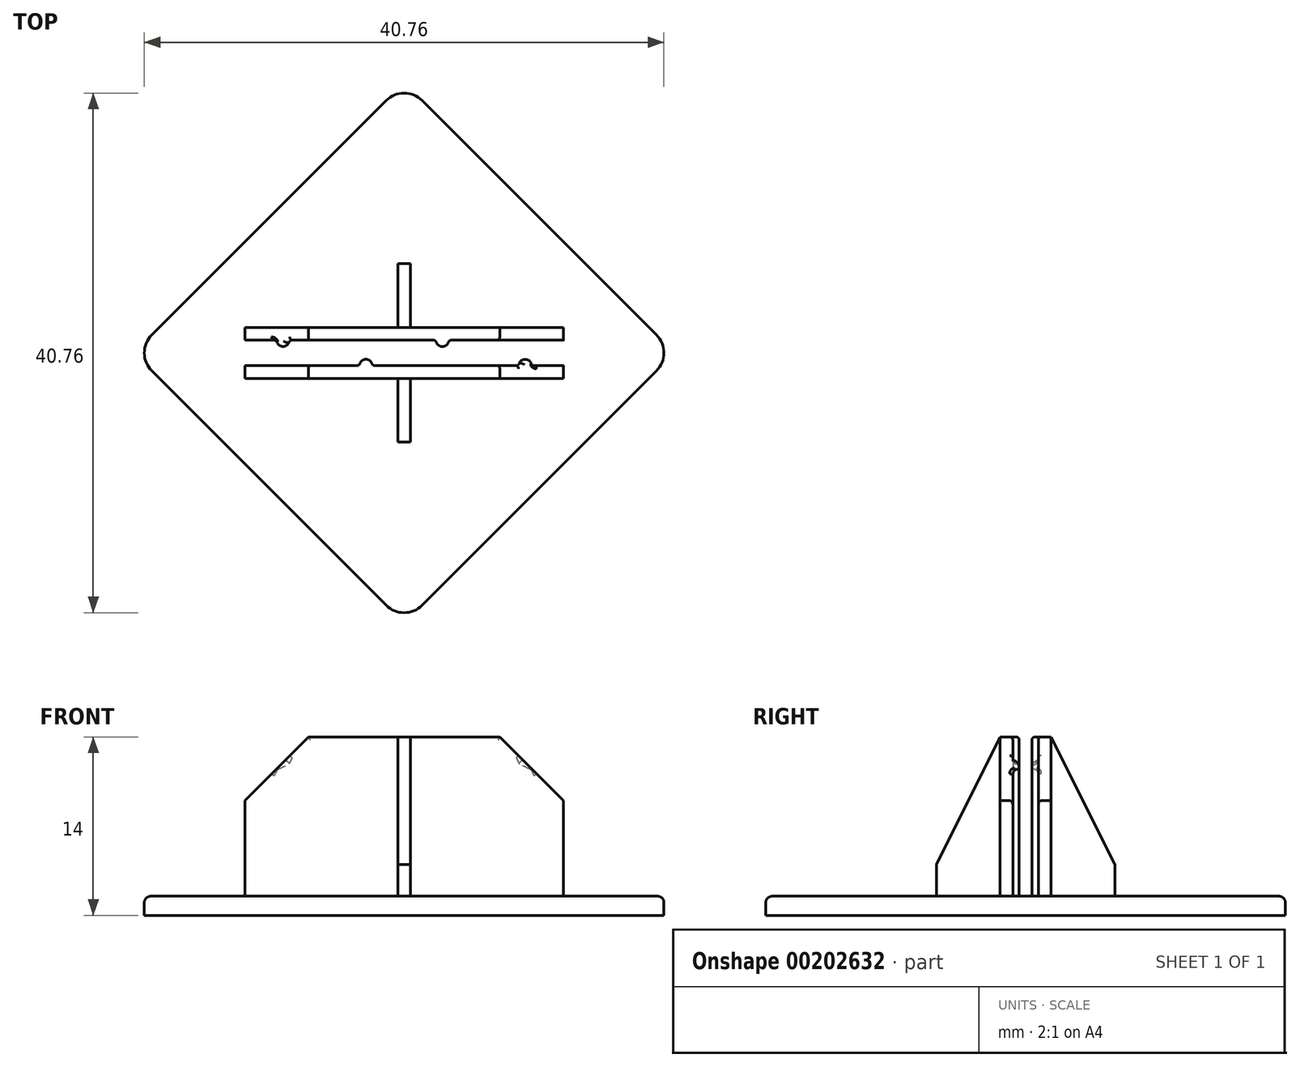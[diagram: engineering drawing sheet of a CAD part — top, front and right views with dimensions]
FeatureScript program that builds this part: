
annotation { "Feature Type Name" : "Feature", "Feature Type Description" : "" }
export const myFeature = defineFeature(function(context is Context, id is Id, definition is map)
    precondition{}
    {
        {
            var Q0;
            Q0=qCreatedBy(makeId("Front.planeOp"),FACE);
            var sketch = newSketch(context, id + "F0", { "sketchPlane" : qUnion([Q0])});
            skLineSegment(sketch, "E0", {"start": v(0, 0) * mm, "end": v(0, 22.97) * mm, "construction": true});
            skSolve(sketch);
        }
        {
            var Q0;
            Q0=qCreatedBy(makeId("Top.planeOp"),FACE);
            var sketch = newSketch(context, id + "F1", { "sketchPlane" : qUnion([Q0])});
            skLineSegment(sketch, "E1.bottom", {"start": v(15, -15) * mm, "end": v(-15, -15) * mm});
            skLineSegment(sketch, "E1.top", {"start": v(15, 15) * mm, "end": v(-15, 15) * mm});
            skLineSegment(sketch, "E1.left", {"start": v(15, -15) * mm, "end": v(15, 15) * mm});
            skLineSegment(sketch, "E1.right", {"start": v(-15, -15) * mm, "end": v(-15, 15) * mm});
            skPoint(sketch, "E1.middle", {"position": v(0, 0) * mm});
            skSolve(sketch);
        }
        {
            var Q0;
            Q0=makeQuery(id+"F1.imprint","IMPRINT",FACE,{"disambiguationData":[TD([[makeQuery(id+"F1.imprint","IMPRINT",EDGE,{"derivedFrom":sQuery(id+"F1.wireOp",EDGE,"E1.bottom")}),-1.0]])]});
            extrude(context, id + "F2", {"entities" : qUnion([Q0]), "depth" : 1.5 * mm});
        }
        {
            var Q0;
            Q0=makeQuery(id+"F2.opExtrude","SWEPT_BODY",BODY,{"disambiguationData":[OSD([sQuery(id+"F1.wireOp",EDGE,"E1.bottom"),sQuery(id+"F1.wireOp",EDGE,"E1.top"),sQuery(id+"F1.wireOp",EDGE,"E1.left"),sQuery(id+"F1.wireOp",EDGE,"E1.right")])]});
            var Q1;
            Q1=sQuery(id+"F0.wireOp",EDGE,"E0");
            transform(context, id + "F3", {"entities" : qUnion([Q0]), "transformType" : TransformType.ROTATION, "transformAxis" : qUnion([Q1]), "angle" : 45 * degree, "makeCopy" : false});
        }
        {
            var Q0;
            Q0=makeQuery(id+"F2.opExtrude","SWEPT_EDGE",EDGE,{"disambiguationData":[OSD([sQuery(id+"F1.wireOp",EDGE,"E1.top"),sQuery(id+"F1.wireOp",EDGE,"E1.right")])]});
            var Q1;
            Q1=makeQuery(id+"F2.opExtrude","SWEPT_EDGE",EDGE,{"disambiguationData":[OSD([sQuery(id+"F1.wireOp",EDGE,"E1.bottom"),sQuery(id+"F1.wireOp",EDGE,"E1.right")])]});
            var Q2;
            Q2=makeQuery(id+"F2.opExtrude","SWEPT_EDGE",EDGE,{"disambiguationData":[OSD([sQuery(id+"F1.wireOp",EDGE,"E1.bottom"),sQuery(id+"F1.wireOp",EDGE,"E1.left")])]});
            var Q3;
            Q3=makeQuery(id+"F2.opExtrude","SWEPT_EDGE",EDGE,{"disambiguationData":[OSD([sQuery(id+"F1.wireOp",EDGE,"E1.top"),sQuery(id+"F1.wireOp",EDGE,"E1.left")])]});
            fillet(context, id + "F4", {"entities" : qUnion([Q0, Q1, Q2, Q3]), "radius" : 2 * mm, "tangentPropagation" : true, "allowEdgeOverflow" : false});
        }
        {
            var Q0;
            Q0=makeQuery(id+"F2.opExtrude","CAP_FACE",FACE,{"disambiguationData":[OSD([sQuery(id+"F1.wireOp",EDGE,"E1.bottom"),sQuery(id+"F1.wireOp",EDGE,"E1.top"),sQuery(id+"F1.wireOp",EDGE,"E1.left"),sQuery(id+"F1.wireOp",EDGE,"E1.right")])],"isStart":false});
            fillet(context, id + "F5", {"entities" : qUnion([Q0]), "radius" : .5 * mm, "tangentPropagation" : true, "allowEdgeOverflow" : false});
        }
        {
            var Q0;
            Q0=makeQuery(id+"F2.opExtrude","CAP_FACE",FACE,{"disambiguationData":[OSD([sQuery(id+"F1.wireOp",EDGE,"E1.bottom"),sQuery(id+"F1.wireOp",EDGE,"E1.top"),sQuery(id+"F1.wireOp",EDGE,"E1.left"),sQuery(id+"F1.wireOp",EDGE,"E1.right")])],"isStart":false});
            var sketch = newSketch(context, id + "F6", { "sketchPlane" : qUnion([Q0])});
            skLineSegment(sketch, "E2", {"start": v(-18.38, 0) * mm, "end": v(18.38, 0) * mm, "construction": true});
            skLineSegment(sketch, "E3.0", {"start": v(-18.38, 1) * mm, "end": v(18.38, 1) * mm, "construction": true});
            skLineSegment(sketch, "E4.0", {"start": v(-18.38, 2) * mm, "end": v(18.38, 2) * mm, "construction": true});
            skLineSegment(sketch, "E5.0", {"start": v(-18.38, 7) * mm, "end": v(18.38, 7) * mm, "construction": true});
            skLineSegment(sketch, "E6", {"start": v(0, 18.38) * mm, "end": v(0, -18.38) * mm, "construction": true});
            skLineSegment(sketch, "E7.0", {"start": v(-12.5, 18.38) * mm, "end": v(-12.5, -18.38) * mm, "construction": true});
            skLineSegment(sketch, "E8.0", {"start": v(12.5, 18.38) * mm, "end": v(12.5, -18.38) * mm, "construction": true});
            skLineSegment(sketch, "E9.0", {"start": v(-0.5, 18.38) * mm, "end": v(-0.5, -18.38) * mm, "construction": true});
            skLineSegment(sketch, "E10.0", {"start": v(0.5, 18.38) * mm, "end": v(0.5, -18.38) * mm, "construction": true});
            skLineSegment(sketch, "E11.0", {"start": v(-9.5, 18.38) * mm, "end": v(-9.5, -18.38) * mm, "construction": true});
            skLineSegment(sketch, "E12.0", {"start": v(3, 18.38) * mm, "end": v(3, -18.38) * mm, "construction": true});
            skCircle(sketch, "E13", {"center": v(-9.5, 1) * mm, "radius": 0.5 * mm});
            skCircle(sketch, "E14", {"center": v(3, 1) * mm, "radius": 0.5 * mm});
            skLineSegment(sketch, "E15", {"start": v(0.5, 7) * mm, "end": v(0.5, 2) * mm});
            skLineSegment(sketch, "E16", {"start": v(0.5, 2) * mm, "end": v(12.5, 2) * mm});
            skLineSegment(sketch, "E17", {"start": v(12.5, 2) * mm, "end": v(12.5, 1) * mm});
            skLineSegment(sketch, "E18", {"start": v(12.5, 1) * mm, "end": v(-12.5, 1) * mm});
            skLineSegment(sketch, "E19", {"start": v(-12.5, 1) * mm, "end": v(-12.5, 2) * mm});
            skLineSegment(sketch, "E20", {"start": v(-12.5, 2) * mm, "end": v(-0.5, 2) * mm});
            skLineSegment(sketch, "E21", {"start": v(-0.5, 2) * mm, "end": v(-0.5, 7) * mm});
            skLineSegment(sketch, "E22", {"start": v(-0.5, 7) * mm, "end": v(0.5, 7) * mm});
            skSolve(sketch);
        }
        {
            var Q0;
            Q0=makeQuery(id+"F6.imprint","IMPRINT",FACE,{"disambiguationData":[TD([[makeQuery(id+"F6.imprint","IMPRINT",EDGE,{"derivedFrom":sQuery(id+"F6.wireOp",EDGE,"E15")}),-1.0]])]});
            var Q1;
            {var subQ0=sQuery(id+"F6.wireOp",EDGE,"E18");var subQ1=sQuery(id+"F6.wireOp",EDGE,"E13");var subQ2=makeQuery(id+"F6.imprint","INTERSECT",VERTEX,{"disambiguationData":[OD(0.0)],"derivedFrom":[subQ1,subQ0]});Q1=makeQuery(id+"F6.imprint","IMPRINT",FACE,{"disambiguationData":[TD([[makeQuery(id+"F6.imprint","IMPRINT",EDGE,{"disambiguationData":[TD([[subQ2,-1.0]])],"derivedFrom":subQ1}),1.0]])]});}
            var Q2;
            {var subQ0=sQuery(id+"F6.wireOp",EDGE,"E18");var subQ1=sQuery(id+"F6.wireOp",EDGE,"E13");var subQ2=makeQuery(id+"F6.imprint","INTERSECT",VERTEX,{"disambiguationData":[OD(0.0)],"derivedFrom":[subQ1,subQ0]});Q2=makeQuery(id+"F6.imprint","IMPRINT",FACE,{"disambiguationData":[TD([[makeQuery(id+"F6.imprint","IMPRINT",EDGE,{"disambiguationData":[TD([[subQ2,1.0]])],"derivedFrom":subQ1}),1.0]])]});}
            var Q3;
            {var subQ0=sQuery(id+"F6.wireOp",EDGE,"E18");var subQ1=sQuery(id+"F6.wireOp",EDGE,"E14");var subQ2=makeQuery(id+"F6.imprint","INTERSECT",VERTEX,{"disambiguationData":[OD(0.0)],"derivedFrom":[subQ1,subQ0]});Q3=makeQuery(id+"F6.imprint","IMPRINT",FACE,{"disambiguationData":[TD([[makeQuery(id+"F6.imprint","IMPRINT",EDGE,{"disambiguationData":[TD([[subQ2,-1.0]])],"derivedFrom":subQ1}),1.0]])]});}
            var Q4;
            {var subQ0=sQuery(id+"F6.wireOp",EDGE,"E18");var subQ1=sQuery(id+"F6.wireOp",EDGE,"E14");var subQ2=makeQuery(id+"F6.imprint","INTERSECT",VERTEX,{"disambiguationData":[OD(0.0)],"derivedFrom":[subQ1,subQ0]});Q4=makeQuery(id+"F6.imprint","IMPRINT",FACE,{"disambiguationData":[TD([[makeQuery(id+"F6.imprint","IMPRINT",EDGE,{"disambiguationData":[TD([[subQ2,1.0]])],"derivedFrom":subQ1}),1.0]])]});}
            extrude(context, id + "F7", {"entities" : qUnion([Q0, Q1, Q2, Q3, Q4]), "depth" : 12.5 * mm});
        }
        {
            var Q0;
            Q0=makeQuery(id+"F7.opExtrude","CAP_EDGE",EDGE,{"disambiguationData":[OSD([sQuery(id+"F6.wireOp",EDGE,"E17")])],"isStart":false});
            var Q1;
            Q1=makeQuery(id+"F7.opExtrude","CAP_EDGE",EDGE,{"disambiguationData":[OSD([sQuery(id+"F6.wireOp",EDGE,"E19")])],"isStart":false});
            chamfer(context, id + "F8", {"entities" : qUnion([Q0, Q1]), "width" : 5 * mm, "tangentPropagation" : true});
        }
        {
            var Q0;
            Q0=makeQuery(id+"F7.opExtrude","CAP_EDGE",EDGE,{"disambiguationData":[OSD([sQuery(id+"F6.wireOp",EDGE,"E22")])],"isStart":false});
            chamfer(context, id + "F9", {"entities" : qUnion([Q0]), "chamferType" : ChamferType.TWO_OFFSETS, "width1" : 10 * mm, "oppositeDirection" : false, "width2" : 5 * mm, "tangentPropagation" : true});
        }
        {
            var Q0;
            {var subQ0=sQuery(id+"F6.wireOp",EDGE,"E18");var subQ1=sQuery(id+"F6.wireOp",EDGE,"E14");Q0=makeQuery(id+"F7.opExtrude","SWEPT_EDGE",EDGE,{"disambiguationData":[OSD([subQ1,subQ0]),TDD([makeQuery(id+"F6.imprint","INTERSECT",VERTEX,{"disambiguationData":[OD(0.0)],"derivedFrom":[subQ1,subQ0]})])]});}
            var Q1;
            {var subQ0=sQuery(id+"F6.wireOp",EDGE,"E18");var subQ1=sQuery(id+"F6.wireOp",EDGE,"E13");Q1=makeQuery(id+"F7.opExtrude","SWEPT_EDGE",EDGE,{"disambiguationData":[OSD([subQ1,subQ0]),TDD([makeQuery(id+"F6.imprint","INTERSECT",VERTEX,{"disambiguationData":[OD(0.0)],"derivedFrom":[subQ1,subQ0]})])]});}
            var Q2;
            {var subQ0=sQuery(id+"F6.wireOp",EDGE,"E18");var subQ1=sQuery(id+"F6.wireOp",EDGE,"E14");Q2=makeQuery(id+"F7.opExtrude","SWEPT_EDGE",EDGE,{"disambiguationData":[OSD([subQ1,subQ0]),TDD([makeQuery(id+"F6.imprint","INTERSECT",VERTEX,{"disambiguationData":[OD(1.0)],"derivedFrom":[subQ1,subQ0]})])]});}
            var Q3;
            {var subQ0=sQuery(id+"F6.wireOp",EDGE,"E18");var subQ1=sQuery(id+"F6.wireOp",EDGE,"E13");Q3=makeQuery(id+"F7.opExtrude","SWEPT_EDGE",EDGE,{"disambiguationData":[OSD([subQ1,subQ0]),TDD([makeQuery(id+"F6.imprint","INTERSECT",VERTEX,{"disambiguationData":[OD(1.0)],"derivedFrom":[subQ1,subQ0]})])]});}
            fillet(context, id + "F10", {"entities" : qUnion([Q0, Q1, Q2, Q3]), "radius" : .25 * mm, "tangentPropagation" : true, "allowEdgeOverflow" : false});
        }
        {
            var Q0;
            {var subQ0=sQuery(id+"F6.wireOp",EDGE,"E19");var subQ1=sQuery(id+"F6.wireOp",EDGE,"E18");Q0=makeQuery(id+"F8.opChamfer","BLEND_EDGE",EDGE,{"blendedFrom":[makeQuery(id+"F7.opExtrude","CAP_EDGE",EDGE,{"disambiguationData":[OSD([subQ0])],"isStart":false}),makeQuery(id+"F7.opExtrude","SWEPT_FACE",FACE,{"disambiguationData":[OSD([subQ1]),TDD([makeQuery(id+"F6.imprint","IMPRINT",EDGE,{"disambiguationData":[TD([[makeQuery(id+"F6.imprint","INTERSECT",VERTEX,{"derivedFrom":[subQ1,subQ0]}),1.0]])],"derivedFrom":subQ1})])]})],"blendedInto":[makeQuery(id+"F7.opExtrude","SWEPT_FACE",FACE,{"disambiguationData":[OSD([subQ1]),TDD([makeQuery(id+"F6.imprint","IMPRINT",EDGE,{"disambiguationData":[TD([[makeQuery(id+"F6.imprint","INTERSECT",VERTEX,{"derivedFrom":[subQ1,subQ0]}),1.0]])],"derivedFrom":subQ1})])]})]});}
            var Q1;
            {var subQ0=sQuery(id+"F6.wireOp",EDGE,"E18");Q1=makeQuery(id+"F7.opExtrude","CAP_EDGE",EDGE,{"disambiguationData":[OSD([subQ0]),TDD([makeQuery(id+"F6.imprint","IMPRINT",EDGE,{"disambiguationData":[TD([[makeQuery(id+"F6.imprint","INTERSECT",VERTEX,{"disambiguationData":[OD(0.0)],"derivedFrom":[sQuery(id+"F6.wireOp",EDGE,"E13"),subQ0]}),1.0]])],"derivedFrom":subQ0})])],"isStart":false});}
            var Q2;
            {var subQ0=sQuery(id+"F6.wireOp",EDGE,"E18");var subQ1=sQuery(id+"F6.wireOp",EDGE,"E17");Q2=makeQuery(id+"F8.opChamfer","BLEND_EDGE",EDGE,{"blendedFrom":[makeQuery(id+"F7.opExtrude","CAP_EDGE",EDGE,{"disambiguationData":[OSD([subQ1])],"isStart":false}),makeQuery(id+"F7.opExtrude","SWEPT_FACE",FACE,{"disambiguationData":[OSD([subQ0]),TDD([makeQuery(id+"F6.imprint","IMPRINT",EDGE,{"disambiguationData":[TD([[makeQuery(id+"F6.imprint","INTERSECT",VERTEX,{"derivedFrom":[subQ1,subQ0]}),-1.0]])],"derivedFrom":subQ0})])]})],"blendedInto":[makeQuery(id+"F7.opExtrude","SWEPT_FACE",FACE,{"disambiguationData":[OSD([subQ0]),TDD([makeQuery(id+"F6.imprint","IMPRINT",EDGE,{"disambiguationData":[TD([[makeQuery(id+"F6.imprint","INTERSECT",VERTEX,{"derivedFrom":[subQ1,subQ0]}),-1.0]])],"derivedFrom":subQ0})])]})]});}
            fillet(context, id + "F11", {"entities" : qUnion([Q0, Q1, Q2]), "radius" : .25 * mm, "tangentPropagation" : true, "allowEdgeOverflow" : false});
        }
        {
            var Q0;
            Q0=makeQuery(id+"F7.opExtrude","SWEPT_BODY",BODY,{"disambiguationData":[OSD([sQuery(id+"F6.wireOp",EDGE,"E13"),sQuery(id+"F6.wireOp",EDGE,"E14"),sQuery(id+"F6.wireOp",EDGE,"E15"),sQuery(id+"F6.wireOp",EDGE,"E16"),sQuery(id+"F6.wireOp",EDGE,"E17"),sQuery(id+"F6.wireOp",EDGE,"E18"),sQuery(id+"F6.wireOp",EDGE,"E19"),sQuery(id+"F6.wireOp",EDGE,"E20"),sQuery(id+"F6.wireOp",EDGE,"E21"),sQuery(id+"F6.wireOp",EDGE,"E22")])]});
            var Q1;
            Q1=sQuery(id+"F0.wireOp",EDGE,"E0");
            transform(context, id + "F12", {"entities" : qUnion([Q0]), "transformType" : TransformType.ROTATION, "transformAxis" : qUnion([Q1]), "angle" : 180 * degree, "makeCopy" : true});
        }
    });
